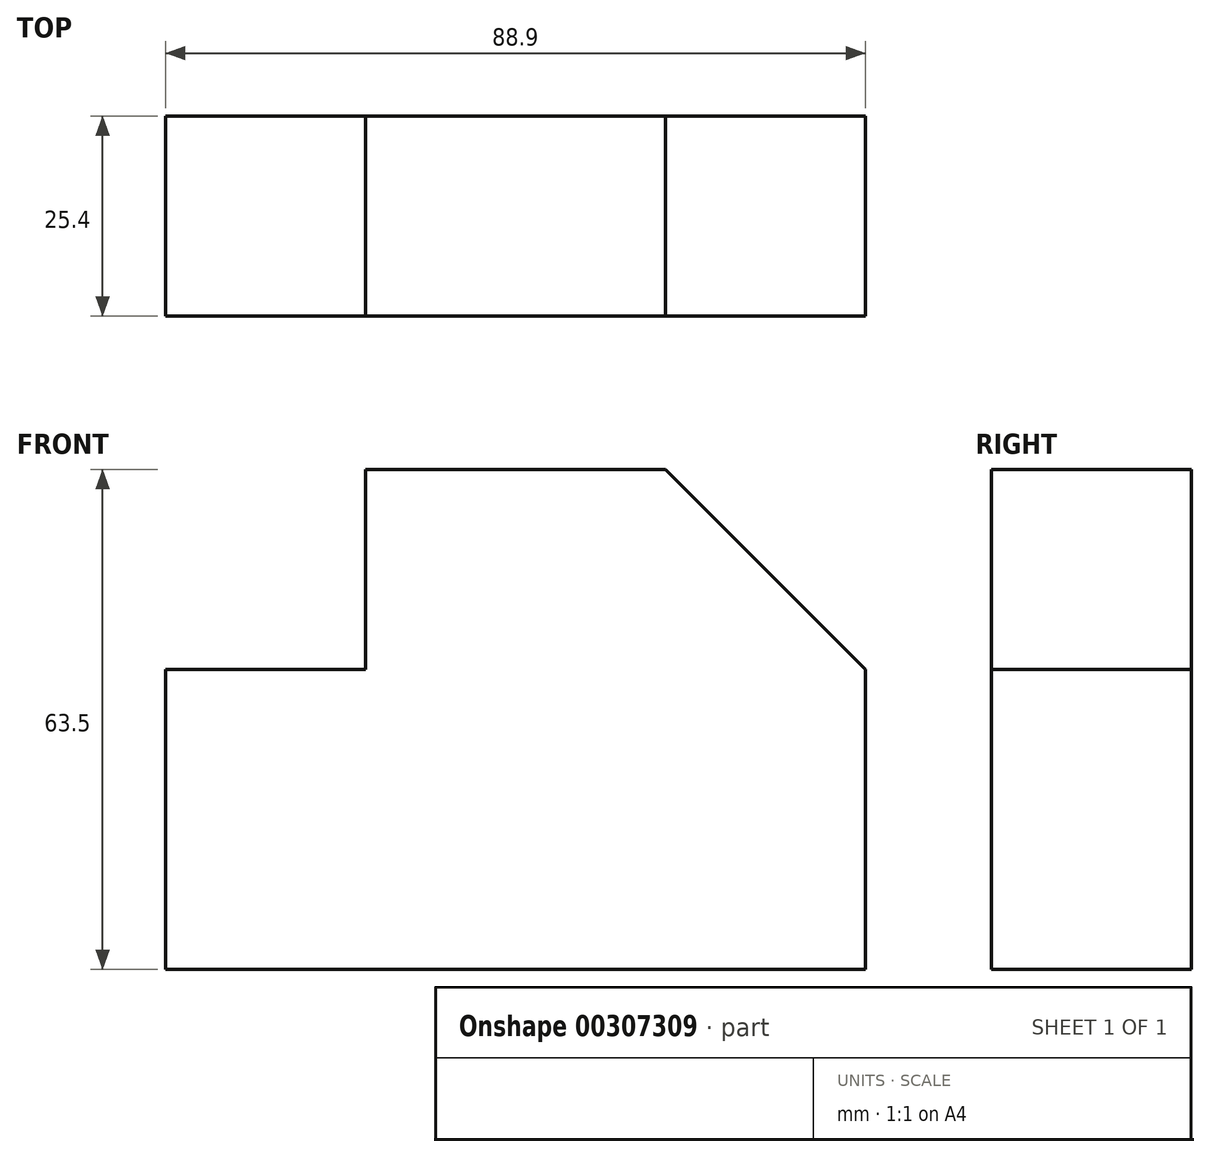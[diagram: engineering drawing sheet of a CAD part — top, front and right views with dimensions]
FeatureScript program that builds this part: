
annotation { "Feature Type Name" : "Feature", "Feature Type Description" : "" }
export const myFeature = defineFeature(function(context is Context, id is Id, definition is map)
    precondition{}
    {
        {
            var Q0;
            Q0=qCreatedBy(makeId("Front.planeOp"),FACE);
            var sketch = newSketch(context, id + "F0", { "sketchPlane" : qUnion([Q0])});
            skLineSegment(sketch, "E0", {"start": v(3.97, 4.5) * mm, "end": v(3.97, -33.6) * mm});
            skLineSegment(sketch, "E1", {"start": v(3.97, -33.6) * mm, "end": v(-84.93, -33.6) * mm});
            skLineSegment(sketch, "E2", {"start": v(-84.93, -33.6) * mm, "end": v(-84.93, 4.5) * mm});
            skLineSegment(sketch, "E3", {"start": v(-84.93, 4.5) * mm, "end": v(-59.53, 4.5) * mm});
            skLineSegment(sketch, "E4", {"start": v(-59.53, 4.5) * mm, "end": v(-59.53, 29.9) * mm});
            skLineSegment(sketch, "E5", {"start": v(-59.53, 29.9) * mm, "end": v(-21.43, 29.9) * mm});
            skLineSegment(sketch, "E6", {"start": v(-21.43, 29.9) * mm, "end": v(3.97, 4.5) * mm});
            skSolve(sketch);
        }
        {
            var Q0;
            Q0=makeQuery(id+"F0.imprint","IMPRINT",FACE,{"disambiguationData":[TD([[makeQuery(id+"F0.imprint","IMPRINT",EDGE,{"derivedFrom":sQuery(id+"F0.wireOp",EDGE,"E0")}),-1.0]])]});
            extrude(context, id + "F1", {"entities" : qUnion([Q0]), "depth" : 25.4 * mm});
        }
    });
